# Revit family: Legrand_Enveloppes_industrielles_Metal_Armoires_Atlantic_Version_verticale
name_source: partatom
category: Equipement électrique
revit_build: Autodesk Revit 2018 (Build: 20170223_1515(x64)
units: mm (PartAtom-declared; Revit-internal decimal feet)

## family parameters
Basée sur le plan de construction = Non
Configuration du panneau = Deux colonnes, circuits au sein
Cote de connecteur circulaire = Utiliser le diamètre
Couper avec des vides une fois chargée = Non
Numéro OmniClass = 23.80.30.11.17
Partagée = Non
Point de calcul de pièce = Non
Titre OmniClass = Distribution Boards and Control Panels
Toujours verticalement = Oui
Type d'élément = Tableau de raccordement

## types (22) — shared parameters
Conditions Générale d'Utilisation = https://export.legrand.com
ETIM Class 6.0 = EC000058
Fabricant = Legrand
IK = 10
IP = 55
Image du type = Atlantic_verticale_035505_pw_234051_pz_18.jpg
Matière = Polyester
RAL = 7035
URL = www.legrand.fr

## per-type parameters (varying)
- Legrand_Enveloppes_industrielles_Metal_Armoires_Atlantic_Version_verticale 035500: Coffret 035500=Oui; Coffret 035502=Non; Coffret 035503=Non; Coffret 035504=Non; Coffret 035507=Non; Coffret 035508=Non; Coffret 035509=Non; Coffret 035512=Non; Coffret 035514=Non; Coffret 035517=Non; Coffret 035518=Non; Coffret 035522=Non; Coffret 035523=Non; Coffret 035526=Non; Coffret 035527=Non; Coffret 035528=Non; Coffret 035529=Non; Coffret 035592=Non; Coffret 035593=Non; Coffret 035595=Non; Coffret 035596=Non; Coffret 035598=Non; Description=Ref 035500 - Legrand_Enveloppes_industrielles_Metal_Armoires_Atlantic_Version_verticale; Hauteur=300 mm; Largeur=200 mm  [stored 0.656168 ft]; Poids=4.20 kg; distance avant zone d'installation=200 mm  [stored 0.656168 ft]; distance coté zone d'installation=160 mm  [stored 0.524934 ft]; largeur zone d'installation=520 mm  [stored 1.70604 ft]; profondeur=160 mm  [stored 0.524934 ft]; profondeur zone d'installation=360 mm
- Legrand_Enveloppes_industrielles_Metal_Armoires_Atlantic_Version_verticale 035502: Coffret 035500=Non; Coffret 035502=Oui; Coffret 035503=Non; Coffret 035504=Non; Coffret 035507=Non; Coffret 035508=Non; Coffret 035509=Non; Coffret 035512=Non; Coffret 035514=Non; Coffret 035517=Non; Coffret 035518=Non; Coffret 035522=Non; Coffret 035523=Non; Coffret 035526=Non; Coffret 035527=Non; Coffret 035528=Non; Coffret 035529=Non; Coffret 035592=Non; Coffret 035593=Non; Coffret 035595=Non; Coffret 035596=Non; Coffret 035598=Non; Description=Ref 035502 - Legrand_Enveloppes_industrielles_Metal_Armoires_Atlantic_Version_verticale; Hauteur=400 mm  [stored 1.31234 ft]; Largeur=300 mm; Poids=6.30 kg; distance avant zone d'installation=300 mm; distance coté zone d'installation=200 mm  [stored 0.656168 ft]; largeur zone d'installation=700 mm  [stored 2.29659 ft]; profondeur=200 mm  [stored 0.656168 ft]; profondeur zone d'installation=500 mm  [stored 1.64042 ft]
- Legrand_Enveloppes_industrielles_Metal_Armoires_Atlantic_Version_verticale 035503: Coffret 035500=Non; Coffret 035502=Non; Coffret 035503=Oui; Coffret 035504=Non; Coffret 035507=Non; Coffret 035508=Non; Coffret 035509=Non; Coffret 035512=Non; Coffret 035514=Non; Coffret 035517=Non; Coffret 035518=Non; Coffret 035522=Non; Coffret 035523=Non; Coffret 035526=Non; Coffret 035527=Non; Coffret 035528=Non; Coffret 035529=Non; Coffret 035592=Non; Coffret 035593=Non; Coffret 035595=Non; Coffret 035596=Non; Coffret 035598=Non; Description=Ref 035503 - Legrand_Enveloppes_industrielles_Metal_Armoires_Atlantic_Version_verticale; Hauteur=500 mm  [stored 1.64042 ft]; Largeur=400 mm  [stored 1.31234 ft]; Poids=9.70 kg; distance avant zone d'installation=400 mm  [stored 1.31234 ft]; distance coté zone d'installation=200 mm  [stored 0.656168 ft]; largeur zone d'installation=800 mm  [stored 2.62467 ft]; profondeur=200 mm  [stored 0.656168 ft]; profondeur zone d'installation=600 mm
- Legrand_Enveloppes_industrielles_Metal_Armoires_Atlantic_Version_verticale 035504: Coffret 035500=Non; Coffret 035502=Non; Coffret 035503=Non; Coffret 035504=Oui; Coffret 035507=Non; Coffret 035508=Non; Coffret 035509=Non; Coffret 035512=Non; Coffret 035514=Non; Coffret 035517=Non; Coffret 035518=Non; Coffret 035522=Non; Coffret 035523=Non; Coffret 035526=Non; Coffret 035527=Non; Coffret 035528=Non; Coffret 035529=Non; Coffret 035592=Non; Coffret 035593=Non; Coffret 035595=Non; Coffret 035596=Non; Coffret 035598=Non; Description=Ref 035504 - Legrand_Enveloppes_industrielles_Metal_Armoires_Atlantic_Version_verticale; Hauteur=600 mm; Largeur=400 mm  [stored 1.31234 ft]; Poids=10.70 kg; distance avant zone d'installation=400 mm  [stored 1.31234 ft]; distance coté zone d'installation=200 mm  [stored 0.656168 ft]; largeur zone d'installation=800 mm  [stored 2.62467 ft]; profondeur=200 mm  [stored 0.656168 ft]; profondeur zone d'installation=600 mm
- Legrand_Enveloppes_industrielles_Metal_Armoires_Atlantic_Version_verticale 035507: Coffret 035500=Non; Coffret 035502=Non; Coffret 035503=Non; Coffret 035504=Non; Coffret 035507=Oui; Coffret 035508=Non; Coffret 035509=Non; Coffret 035512=Non; Coffret 035514=Non; Coffret 035517=Non; Coffret 035518=Non; Coffret 035522=Non; Coffret 035523=Non; Coffret 035526=Non; Coffret 035527=Non; Coffret 035528=Non; Coffret 035529=Non; Coffret 035592=Non; Coffret 035593=Non; Coffret 035595=Non; Coffret 035596=Non; Coffret 035598=Non; Description=Ref 035507 - Legrand_Enveloppes_industrielles_Metal_Armoires_Atlantic_Version_verticale; Hauteur=500 mm  [stored 1.64042 ft]; Largeur=400 mm  [stored 1.31234 ft]; Poids=10.70 kg; distance avant zone d'installation=400 mm  [stored 1.31234 ft]; distance coté zone d'installation=250 mm  [stored 0.82021 ft]; largeur zone d'installation=900 mm  [stored 2.95276 ft]; profondeur=250 mm  [stored 0.82021 ft]; profondeur zone d'installation=650 mm  [stored 2.13255 ft]
- Legrand_Enveloppes_industrielles_Metal_Armoires_Atlantic_Version_verticale 035508: Coffret 035500=Non; Coffret 035502=Non; Coffret 035503=Non; Coffret 035504=Non; Coffret 035507=Non; Coffret 035508=Oui; Coffret 035509=Non; Coffret 035512=Non; Coffret 035514=Non; Coffret 035517=Non; Coffret 035518=Non; Coffret 035522=Non; Coffret 035523=Non; Coffret 035526=Non; Coffret 035527=Non; Coffret 035528=Non; Coffret 035529=Non; Coffret 035592=Non; Coffret 035593=Non; Coffret 035595=Non; Coffret 035596=Non; Coffret 035598=Non; Description=Ref 035508 - Legrand_Enveloppes_industrielles_Metal_Armoires_Atlantic_Version_verticale; Hauteur=600 mm; Largeur=400 mm  [stored 1.31234 ft]; Poids=12.00 kg; distance avant zone d'installation=400 mm  [stored 1.31234 ft]; distance coté zone d'installation=250 mm  [stored 0.82021 ft]; largeur zone d'installation=900 mm  [stored 2.95276 ft]; profondeur=250 mm  [stored 0.82021 ft]; profondeur zone d'installation=650 mm  [stored 2.13255 ft]
- Legrand_Enveloppes_industrielles_Metal_Armoires_Atlantic_Version_verticale 035509: Coffret 035500=Non; Coffret 035502=Non; Coffret 035503=Non; Coffret 035504=Non; Coffret 035507=Non; Coffret 035508=Non; Coffret 035509=Oui; Coffret 035512=Non; Coffret 035514=Non; Coffret 035517=Non; Coffret 035518=Non; Coffret 035522=Non; Coffret 035523=Non; Coffret 035526=Non; Coffret 035527=Non; Coffret 035528=Non; Coffret 035529=Non; Coffret 035592=Non; Coffret 035593=Non; Coffret 035595=Non; Coffret 035596=Non; Coffret 035598=Non; Description=Ref 035509 - Legrand_Enveloppes_industrielles_Metal_Armoires_Atlantic_Version_verticale; Hauteur=400 mm  [stored 1.31234 ft]; Largeur=300 mm; Poids=6.30 kg; distance avant zone d'installation=300 mm; distance coté zone d'installation=160 mm  [stored 0.524934 ft]; largeur zone d'installation=620 mm; profondeur=160 mm  [stored 0.524934 ft]; profondeur zone d'installation=460 mm
- Legrand_Enveloppes_industrielles_Metal_Armoires_Atlantic_Version_verticale 035512: Coffret 035500=Non; Coffret 035502=Non; Coffret 035503=Non; Coffret 035504=Non; Coffret 035507=Non; Coffret 035508=Non; Coffret 035509=Non; Coffret 035512=Oui; Coffret 035514=Non; Coffret 035517=Non; Coffret 035518=Non; Coffret 035522=Non; Coffret 035523=Non; Coffret 035526=Non; Coffret 035527=Non; Coffret 035528=Non; Coffret 035529=Non; Coffret 035592=Non; Coffret 035593=Non; Coffret 035595=Non; Coffret 035596=Non; Coffret 035598=Non; Description=Ref 035512 - Legrand_Enveloppes_industrielles_Metal_Armoires_Atlantic_Version_verticale; Hauteur=700 mm  [stored 2.29659 ft]; Largeur=500 mm  [stored 1.64042 ft]; Poids=16.50 kg; distance avant zone d'installation=500 mm  [stored 1.64042 ft]; distance coté zone d'installation=250 mm  [stored 0.82021 ft]; largeur zone d'installation=1000 mm  [stored 3.28084 ft]; profondeur=250 mm  [stored 0.82021 ft]; profondeur zone d'installation=750 mm  [stored 2.46063 ft]
- Legrand_Enveloppes_industrielles_Metal_Armoires_Atlantic_Version_verticale 035514: Coffret 035500=Non; Coffret 035502=Non; Coffret 035503=Non; Coffret 035504=Non; Coffret 035507=Non; Coffret 035508=Non; Coffret 035509=Non; Coffret 035512=Non; Coffret 035514=Oui; Coffret 035517=Non; Coffret 035518=Non; Coffret 035522=Non; Coffret 035523=Non; Coffret 035526=Non; Coffret 035527=Non; Coffret 035528=Non; Coffret 035529=Non; Coffret 035592=Non; Coffret 035593=Non; Coffret 035595=Non; Coffret 035596=Non; Coffret 035598=Non; Description=Ref 035514 - Legrand_Enveloppes_industrielles_Metal_Armoires_Atlantic_Version_verticale; Hauteur=800 mm  [stored 2.62467 ft]; Largeur=600 mm; Poids=18.80 kg; distance avant zone d'installation=600 mm; distance coté zone d'installation=250 mm  [stored 0.82021 ft]; largeur zone d'installation=1100 mm; profondeur=250 mm  [stored 0.82021 ft]; profondeur zone d'installation=850 mm  [stored 2.78871 ft]
- Legrand_Enveloppes_industrielles_Metal_Armoires_Atlantic_Version_verticale 035517: Coffret 035500=Non; Coffret 035502=Non; Coffret 035503=Non; Coffret 035504=Non; Coffret 035507=Non; Coffret 035508=Non; Coffret 035509=Non; Coffret 035512=Non; Coffret 035514=Non; Coffret 035517=Oui; Coffret 035518=Non; Coffret 035522=Non; Coffret 035523=Non; Coffret 035526=Non; Coffret 035527=Non; Coffret 035528=Non; Coffret 035529=Non; Coffret 035592=Non; Coffret 035593=Non; Coffret 035595=Non; Coffret 035596=Non; Coffret 035598=Non; Description=Ref 035517 - Legrand_Enveloppes_industrielles_Metal_Armoires_Atlantic_Version_verticale; Hauteur=1000 mm  [stored 3.28084 ft]; Largeur=600 mm; Poids=24.00 kg; distance avant zone d'installation=600 mm; distance coté zone d'installation=250 mm  [stored 0.82021 ft]; largeur zone d'installation=1100 mm; profondeur=250 mm  [stored 0.82021 ft]; profondeur zone d'installation=850 mm  [stored 2.78871 ft]
- Legrand_Enveloppes_industrielles_Metal_Armoires_Atlantic_Version_verticale 035518: Coffret 035500=Non; Coffret 035502=Non; Coffret 035503=Non; Coffret 035504=Non; Coffret 035507=Non; Coffret 035508=Non; Coffret 035509=Non; Coffret 035512=Non; Coffret 035514=Non; Coffret 035517=Non; Coffret 035518=Oui; Coffret 035522=Non; Coffret 035523=Non; Coffret 035526=Non; Coffret 035527=Non; Coffret 035528=Non; Coffret 035529=Non; Coffret 035592=Non; Coffret 035593=Non; Coffret 035595=Non; Coffret 035596=Non; Coffret 035598=Non; Description=Ref 035518 - Legrand_Enveloppes_industrielles_Metal_Armoires_Atlantic_Version_verticale; Hauteur=1000 mm  [stored 3.28084 ft]; Largeur=800 mm  [stored 2.62467 ft]; Poids=36.40 kg; distance avant zone d'installation=800 mm  [stored 2.62467 ft]; distance coté zone d'installation=250 mm  [stored 0.82021 ft]; largeur zone d'installation=1300 mm  [stored 4.26509 ft]; profondeur=250 mm  [stored 0.82021 ft]; profondeur zone d'installation=1050 mm
- Legrand_Enveloppes_industrielles_Metal_Armoires_Atlantic_Version_verticale 035522: Coffret 035500=Non; Coffret 035502=Non; Coffret 035503=Non; Coffret 035504=Non; Coffret 035507=Non; Coffret 035508=Non; Coffret 035509=Non; Coffret 035512=Non; Coffret 035514=Non; Coffret 035517=Non; Coffret 035518=Non; Coffret 035522=Oui; Coffret 035523=Non; Coffret 035526=Non; Coffret 035527=Non; Coffret 035528=Non; Coffret 035529=Non; Coffret 035592=Non; Coffret 035593=Non; Coffret 035595=Non; Coffret 035596=Non; Coffret 035598=Non; Description=Ref 035522 - Legrand_Enveloppes_industrielles_Metal_Armoires_Atlantic_Version_verticale; Hauteur=700 mm  [stored 2.29659 ft]; Largeur=500 mm  [stored 1.64042 ft]; Poids=23.00 kg; distance avant zone d'installation=500 mm  [stored 1.64042 ft]; distance coté zone d'installation=300 mm; largeur zone d'installation=1100 mm; profondeur=300 mm; profondeur zone d'installation=800 mm  [stored 2.62467 ft]
- Legrand_Enveloppes_industrielles_Metal_Armoires_Atlantic_Version_verticale 035523: Coffret 035500=Non; Coffret 035502=Non; Coffret 035503=Non; Coffret 035504=Non; Coffret 035507=Non; Coffret 035508=Non; Coffret 035509=Non; Coffret 035512=Non; Coffret 035514=Non; Coffret 035517=Non; Coffret 035518=Non; Coffret 035522=Non; Coffret 035523=Oui; Coffret 035526=Non; Coffret 035527=Non; Coffret 035528=Non; Coffret 035529=Non; Coffret 035592=Non; Coffret 035593=Non; Coffret 035595=Non; Coffret 035596=Non; Coffret 035598=Non; Description=Ref 035523 - Legrand_Enveloppes_industrielles_Metal_Armoires_Atlantic_Version_verticale; Hauteur=800 mm  [stored 2.62467 ft]; Largeur=600 mm; Poids=28.80 kg; distance avant zone d'installation=600 mm; distance coté zone d'installation=300 mm; largeur zone d'installation=1200 mm; profondeur=300 mm; profondeur zone d'installation=900 mm  [stored 2.95276 ft]
- Legrand_Enveloppes_industrielles_Metal_Armoires_Atlantic_Version_verticale 035526: Coffret 035500=Non; Coffret 035502=Non; Coffret 035503=Non; Coffret 035504=Non; Coffret 035507=Non; Coffret 035508=Non; Coffret 035509=Non; Coffret 035512=Non; Coffret 035514=Non; Coffret 035517=Non; Coffret 035518=Non; Coffret 035522=Non; Coffret 035523=Non; Coffret 035526=Oui; Coffret 035527=Non; Coffret 035528=Non; Coffret 035529=Non; Coffret 035592=Non; Coffret 035593=Non; Coffret 035595=Non; Coffret 035596=Non; Coffret 035598=Non; Description=Ref 035526 - Legrand_Enveloppes_industrielles_Metal_Armoires_Atlantic_Version_verticale; Hauteur=1000 mm  [stored 3.28084 ft]; Largeur=600 mm; Poids=33.30 kg; distance avant zone d'installation=600 mm; distance coté zone d'installation=300 mm; largeur zone d'installation=1200 mm; profondeur=300 mm; profondeur zone d'installation=900 mm  [stored 2.95276 ft]
- Legrand_Enveloppes_industrielles_Metal_Armoires_Atlantic_Version_verticale 035527: Coffret 035500=Non; Coffret 035502=Non; Coffret 035503=Non; Coffret 035504=Non; Coffret 035507=Non; Coffret 035508=Non; Coffret 035509=Non; Coffret 035512=Non; Coffret 035514=Non; Coffret 035517=Non; Coffret 035518=Non; Coffret 035522=Non; Coffret 035523=Non; Coffret 035526=Non; Coffret 035527=Oui; Coffret 035528=Non; Coffret 035529=Non; Coffret 035592=Non; Coffret 035593=Non; Coffret 035595=Non; Coffret 035596=Non; Coffret 035598=Non; Description=Ref 035527 - Legrand_Enveloppes_industrielles_Metal_Armoires_Atlantic_Version_verticale; Hauteur=1000 mm  [stored 3.28084 ft]; Largeur=800 mm  [stored 2.62467 ft]; Poids=42.00 kg; distance avant zone d'installation=800 mm  [stored 2.62467 ft]; distance coté zone d'installation=300 mm; largeur zone d'installation=1400 mm  [stored 4.59318 ft]; profondeur=300 mm; profondeur zone d'installation=1100 mm
- Legrand_Enveloppes_industrielles_Metal_Armoires_Atlantic_Version_verticale 035528: Coffret 035500=Non; Coffret 035502=Non; Coffret 035503=Non; Coffret 035504=Non; Coffret 035507=Non; Coffret 035508=Non; Coffret 035509=Non; Coffret 035512=Non; Coffret 035514=Non; Coffret 035517=Non; Coffret 035518=Non; Coffret 035522=Non; Coffret 035523=Non; Coffret 035526=Non; Coffret 035527=Non; Coffret 035528=Oui; Coffret 035529=Non; Coffret 035592=Non; Coffret 035593=Non; Coffret 035595=Non; Coffret 035596=Non; Coffret 035598=Non; Description=Ref 035528 - Legrand_Enveloppes_industrielles_Metal_Armoires_Atlantic_Version_verticale; Hauteur=800 mm  [stored 2.62467 ft]; Largeur=600 mm; Poids=31.00 kg; distance avant zone d'installation=600 mm; distance coté zone d'installation=400 mm  [stored 1.31234 ft]; largeur zone d'installation=1400 mm  [stored 4.59318 ft]; profondeur=400 mm  [stored 1.31234 ft]; profondeur zone d'installation=1000 mm  [stored 3.28084 ft]
- Legrand_Enveloppes_industrielles_Metal_Armoires_Atlantic_Version_verticale 035529: Coffret 035500=Non; Coffret 035502=Non; Coffret 035503=Non; Coffret 035504=Non; Coffret 035507=Non; Coffret 035508=Non; Coffret 035509=Non; Coffret 035512=Non; Coffret 035514=Non; Coffret 035517=Non; Coffret 035518=Non; Coffret 035522=Non; Coffret 035523=Non; Coffret 035526=Non; Coffret 035527=Non; Coffret 035528=Non; Coffret 035529=Oui; Coffret 035592=Non; Coffret 035593=Non; Coffret 035595=Non; Coffret 035596=Non; Coffret 035598=Non; Description=Ref 035529 - Legrand_Enveloppes_industrielles_Metal_Armoires_Atlantic_Version_verticale; Hauteur=1000 mm  [stored 3.28084 ft]; Largeur=800 mm  [stored 2.62467 ft]; Poids=45.00 kg; distance avant zone d'installation=800 mm  [stored 2.62467 ft]; distance coté zone d'installation=400 mm  [stored 1.31234 ft]; largeur zone d'installation=1600 mm  [stored 5.24934 ft]; profondeur=400 mm  [stored 1.31234 ft]; profondeur zone d'installation=1200 mm
- Legrand_Enveloppes_industrielles_Metal_Armoires_Atlantic_Version_verticale 035592: Coffret 035500=Non; Coffret 035502=Non; Coffret 035503=Non; Coffret 035504=Non; Coffret 035507=Non; Coffret 035508=Non; Coffret 035509=Non; Coffret 035512=Non; Coffret 035514=Non; Coffret 035517=Non; Coffret 035518=Non; Coffret 035522=Non; Coffret 035523=Non; Coffret 035526=Non; Coffret 035527=Non; Coffret 035528=Non; Coffret 035529=Non; Coffret 035592=Oui; Coffret 035593=Non; Coffret 035595=Non; Coffret 035596=Non; Coffret 035598=Non; Description=Ref 035592 - Legrand_Enveloppes_industrielles_Metal_Armoires_Atlantic_Version_verticale; Hauteur=1200 mm; Largeur=800 mm  [stored 2.62467 ft]; Poids=49.60 kg; distance avant zone d'installation=800 mm  [stored 2.62467 ft]; distance coté zone d'installation=300 mm; largeur zone d'installation=1400 mm  [stored 4.59318 ft]; profondeur=300 mm; profondeur zone d'installation=1100 mm
- Legrand_Enveloppes_industrielles_Metal_Armoires_Atlantic_Version_verticale 035593: Coffret 035500=Non; Coffret 035502=Non; Coffret 035503=Non; Coffret 035504=Non; Coffret 035507=Non; Coffret 035508=Non; Coffret 035509=Non; Coffret 035512=Non; Coffret 035514=Non; Coffret 035517=Non; Coffret 035518=Non; Coffret 035522=Non; Coffret 035523=Non; Coffret 035526=Non; Coffret 035527=Non; Coffret 035528=Non; Coffret 035529=Non; Coffret 035592=Non; Coffret 035593=Oui; Coffret 035595=Non; Coffret 035596=Non; Coffret 035598=Non; Description=Ref 035593 - Legrand_Enveloppes_industrielles_Metal_Armoires_Atlantic_Version_verticale; Hauteur=1200 mm; Largeur=1000 mm  [stored 3.28084 ft]; Poids=62.20 kg; distance avant zone d'installation=1000 mm  [stored 3.28084 ft]; distance coté zone d'installation=300 mm; largeur zone d'installation=1600 mm  [stored 5.24934 ft]; profondeur=300 mm; profondeur zone d'installation=1300 mm  [stored 4.26509 ft]
- Legrand_Enveloppes_industrielles_Metal_Armoires_Atlantic_Version_verticale 035595: Coffret 035500=Non; Coffret 035502=Non; Coffret 035503=Non; Coffret 035504=Non; Coffret 035507=Non; Coffret 035508=Non; Coffret 035509=Non; Coffret 035512=Non; Coffret 035514=Non; Coffret 035517=Non; Coffret 035518=Non; Coffret 035522=Non; Coffret 035523=Non; Coffret 035526=Non; Coffret 035527=Non; Coffret 035528=Non; Coffret 035529=Non; Coffret 035592=Non; Coffret 035593=Non; Coffret 035595=Oui; Coffret 035596=Non; Coffret 035598=Non; Description=Ref 035595 - Legrand_Enveloppes_industrielles_Metal_Armoires_Atlantic_Version_verticale; Hauteur=1400 mm  [stored 4.59318 ft]; Largeur=1000 mm  [stored 3.28084 ft]; Poids=71.00 kg; distance avant zone d'installation=1000 mm  [stored 3.28084 ft]; distance coté zone d'installation=300 mm; largeur zone d'installation=1600 mm  [stored 5.24934 ft]; profondeur=300 mm; profondeur zone d'installation=1300 mm  [stored 4.26509 ft]
- Legrand_Enveloppes_industrielles_Metal_Armoires_Atlantic_Version_verticale 035596: Coffret 035500=Non; Coffret 035502=Non; Coffret 035503=Non; Coffret 035504=Non; Coffret 035507=Non; Coffret 035508=Non; Coffret 035509=Non; Coffret 035512=Non; Coffret 035514=Non; Coffret 035517=Non; Coffret 035518=Non; Coffret 035522=Non; Coffret 035523=Non; Coffret 035526=Non; Coffret 035527=Non; Coffret 035528=Non; Coffret 035529=Non; Coffret 035592=Non; Coffret 035593=Non; Coffret 035595=Non; Coffret 035596=Oui; Coffret 035598=Non; Description=Ref 035596 - Legrand_Enveloppes_industrielles_Metal_Armoires_Atlantic_Version_verticale; Hauteur=1200 mm; Largeur=800 mm  [stored 2.62467 ft]; Poids=57.00 kg; distance avant zone d'installation=800 mm  [stored 2.62467 ft]; distance coté zone d'installation=400 mm  [stored 1.31234 ft]; largeur zone d'installation=1600 mm  [stored 5.24934 ft]; profondeur=400 mm  [stored 1.31234 ft]; profondeur zone d'installation=1200 mm
- Legrand_Enveloppes_industrielles_Metal_Armoires_Atlantic_Version_verticale 035598: Coffret 035500=Non; Coffret 035502=Non; Coffret 035503=Non; Coffret 035504=Non; Coffret 035507=Non; Coffret 035508=Non; Coffret 035509=Non; Coffret 035512=Non; Coffret 035514=Non; Coffret 035517=Non; Coffret 035518=Non; Coffret 035522=Non; Coffret 035523=Non; Coffret 035526=Non; Coffret 035527=Non; Coffret 035528=Non; Coffret 035529=Non; Coffret 035592=Non; Coffret 035593=Non; Coffret 035595=Non; Coffret 035596=Non; Coffret 035598=Oui; Description=Ref 035598 - Legrand_Enveloppes_industrielles_Metal_Armoires_Atlantic_Version_verticale; Hauteur=1400 mm  [stored 4.59318 ft]; Largeur=800 mm  [stored 2.62467 ft]; Poids=64.00 kg; distance avant zone d'installation=800 mm  [stored 2.62467 ft]; distance coté zone d'installation=400 mm  [stored 1.31234 ft]; largeur zone d'installation=1600 mm  [stored 5.24934 ft]; profondeur=400 mm  [stored 1.31234 ft]; profondeur zone d'installation=1200 mm

note: [stored X ft] marks values corroborated as IEEE doubles in the binary element streams (Revit-internal decimal feet)
